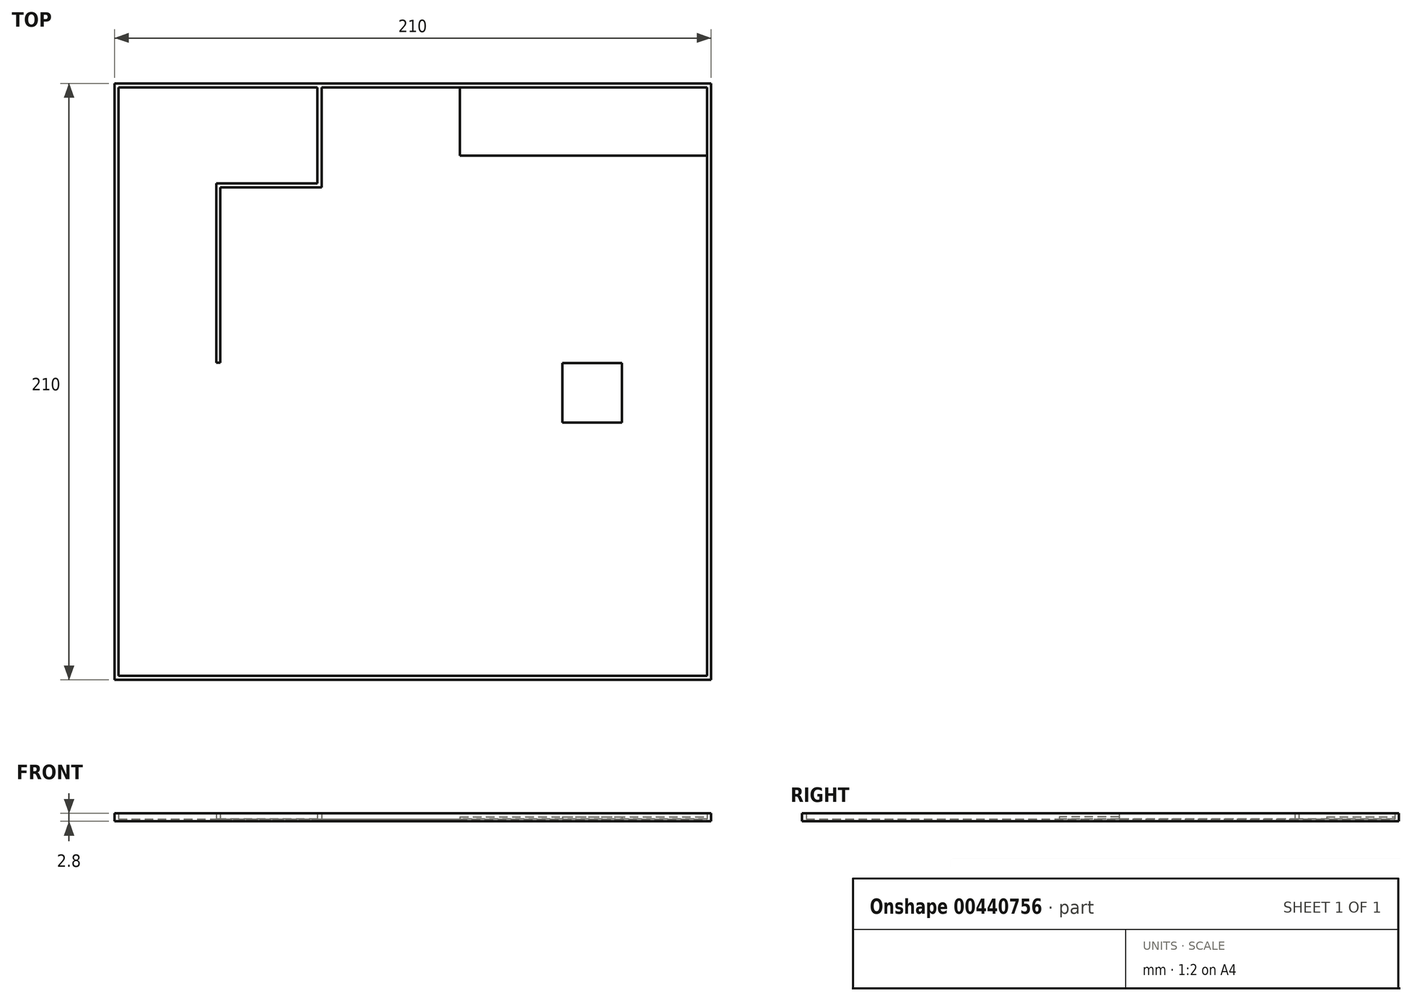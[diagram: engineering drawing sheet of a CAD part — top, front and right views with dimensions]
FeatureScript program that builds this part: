
annotation { "Feature Type Name" : "Feature", "Feature Type Description" : "" }
export const myFeature = defineFeature(function(context is Context, id is Id, definition is map)
    precondition{}
    {
        {
            var Q0;
            Q0=qCreatedBy(makeId("Top.planeOp"),FACE);
            var sketch = newSketch(context, id + "F0", { "sketchPlane" : qUnion([Q0])});
            skLineSegment(sketch, "E0.bottom", {"start": v(0, 0) * mm, "end": v(210, 0) * mm});
            skLineSegment(sketch, "E0.top", {"start": v(0, 210) * mm, "end": v(210, 210) * mm});
            skLineSegment(sketch, "E0.left", {"start": v(0, 0) * mm, "end": v(0, 210) * mm});
            skLineSegment(sketch, "E0.right", {"start": v(210, 0) * mm, "end": v(210, 210) * mm});
            skSolve(sketch);
        }
        {
            var Q0;
            Q0=makeQuery(id+"F0.imprint","IMPRINT",FACE,{"disambiguationData":[TD([[makeQuery(id+"F0.imprint","IMPRINT",EDGE,{"derivedFrom":sQuery(id+"F0.wireOp",EDGE,"E0.bottom")}),1.0]])]});
            extrude(context, id + "F1", {"entities" : qUnion([Q0]), "depth" : .8 * mm});
        }
        {
            var Q0;
            Q0=makeQuery(id+"F1.opExtrude","CAP_FACE",FACE,{"disambiguationData":[OSD([sQuery(id+"F0.wireOp",EDGE,"E0.bottom"),sQuery(id+"F0.wireOp",EDGE,"E0.top"),sQuery(id+"F0.wireOp",EDGE,"E0.left"),sQuery(id+"F0.wireOp",EDGE,"E0.right")])],"isStart":false});
            var sketch = newSketch(context, id + "F2", { "sketchPlane" : qUnion([Q0])});
            skLineSegment(sketch, "E1.0", {"start": v(1.44, 1.44) * mm, "end": v(208.56, 1.44) * mm});
            skLineSegment(sketch, "E1.1", {"start": v(1.44, 1.44) * mm, "end": v(1.44, 208.56) * mm});
            skLineSegment(sketch, "E1.2", {"start": v(1.44, 208.56) * mm, "end": v(208.56, 208.56) * mm});
            skLineSegment(sketch, "E1.3", {"start": v(208.56, 1.44) * mm, "end": v(208.56, 208.56) * mm});
            skLineSegment(sketch, "E2.0", {"start": v(0, 0) * mm, "end": v(210, 0) * mm});
            skLineSegment(sketch, "E3.0", {"start": v(0, 0) * mm, "end": v(0, 210) * mm});
            skLineSegment(sketch, "E4.0", {"start": v(0, 210) * mm, "end": v(210, 210) * mm});
            skLineSegment(sketch, "E5.0", {"start": v(210, 0) * mm, "end": v(210, 210) * mm});
            skSolve(sketch);
        }
        {
            var Q0;
            Q0=qSketchRegion(id+"F2",true);
            extrude(context, id + "F3", {"entities" : qUnion([Q0]), "operationType" : NewBodyOperationType.ADD, "depth" : 2 * mm});
        }
        {
            var Q0;
            Q0=makeQuery(id+"F1.opExtrude","CAP_FACE",FACE,{"disambiguationData":[OSD([sQuery(id+"F0.wireOp",EDGE,"E0.bottom"),sQuery(id+"F0.wireOp",EDGE,"E0.top"),sQuery(id+"F0.wireOp",EDGE,"E0.left"),sQuery(id+"F0.wireOp",EDGE,"E0.right")])],"isStart":false});
            var sketch = newSketch(context, id + "F4", { "sketchPlane" : qUnion([Q0])});
            skLineSegment(sketch, "E6", {"start": v(72.89, 208.56) * mm, "end": v(72.89, 173.37) * mm});
            skLineSegment(sketch, "E7", {"start": v(35.77, 174.81) * mm, "end": v(35.77, 111.64) * mm});
            skLineSegment(sketch, "E8", {"start": v(37.2, 111.64) * mm, "end": v(37.2, 173.37) * mm});
            skLineSegment(sketch, "E9", {"start": v(37.2, 173.37) * mm, "end": v(72.89, 173.37) * mm});
            skLineSegment(sketch, "E10", {"start": v(71.45, 208.56) * mm, "end": v(72.89, 208.56) * mm});
            skLineSegment(sketch, "E11", {"start": v(71.45, 208.56) * mm, "end": v(71.45, 174.81) * mm});
            skLineSegment(sketch, "E12.trimOffspring", {"start": v(71.45, 174.81) * mm, "end": v(35.77, 174.81) * mm});
            skLineSegment(sketch, "E13", {"start": v(35.77, 111.64) * mm, "end": v(37.2, 111.64) * mm});
            skSolve(sketch);
        }
        {
            var Q0;
            Q0=qSketchRegion(id+"F4",true);
            var Q1;
            Q1=makeQuery(id+"F3.opExtrude","CAP_FACE",FACE,{"disambiguationData":[OSD([sQuery(id+"F2.wireOp",EDGE,"E1.0"),sQuery(id+"F2.wireOp",EDGE,"E1.1"),sQuery(id+"F2.wireOp",EDGE,"E1.2"),sQuery(id+"F2.wireOp",EDGE,"E1.3"),sQuery(id+"F2.wireOp",EDGE,"E2.0"),sQuery(id+"F2.wireOp",EDGE,"E3.0"),sQuery(id+"F2.wireOp",EDGE,"E4.0"),sQuery(id+"F2.wireOp",EDGE,"E5.0")])],"isStart":false});
            extrude(context, id + "F5", {"entities" : qUnion([Q0]), "operationType" : NewBodyOperationType.ADD, "endBound" : BoundingType.UP_TO_SURFACE, "endBoundEntityFace" : qUnion([Q1]), "depth" : 25 * mm});
        }
        {
            var Q0;
            Q0=makeQuery(id+"F1.opExtrude","CAP_FACE",FACE,{"disambiguationData":[OSD([sQuery(id+"F0.wireOp",EDGE,"E0.bottom"),sQuery(id+"F0.wireOp",EDGE,"E0.top"),sQuery(id+"F0.wireOp",EDGE,"E0.left"),sQuery(id+"F0.wireOp",EDGE,"E0.right")])],"isStart":false});
            var sketch = newSketch(context, id + "F6", { "sketchPlane" : qUnion([Q0])});
            skLineSegment(sketch, "E14.bottom", {"start": v(208.56, 208.56) * mm, "end": v(121.56, 208.56) * mm});
            skLineSegment(sketch, "E14.top", {"start": v(208.56, 184.56) * mm, "end": v(121.56, 184.56) * mm});
            skLineSegment(sketch, "E14.left", {"start": v(208.56, 208.56) * mm, "end": v(208.56, 184.56) * mm});
            skLineSegment(sketch, "E14.right", {"start": v(121.56, 208.56) * mm, "end": v(121.56, 184.56) * mm});
            skLineSegment(sketch, "E15.bottom", {"start": v(157.56, 111.56) * mm, "end": v(178.56, 111.56) * mm});
            skLineSegment(sketch, "E15.top", {"start": v(157.56, 90.56) * mm, "end": v(178.56, 90.56) * mm});
            skLineSegment(sketch, "E15.left", {"start": v(157.56, 111.56) * mm, "end": v(157.56, 90.56) * mm});
            skLineSegment(sketch, "E15.right", {"start": v(178.56, 111.56) * mm, "end": v(178.56, 90.56) * mm});
            skSolve(sketch);
        }
        {
            var Q0;
            Q0=qSketchRegion(id+"F6",true);
            extrude(context, id + "F7", {"entities" : qUnion([Q0]), "operationType" : NewBodyOperationType.ADD, "depth" : .8 * mm});
        }
    });
